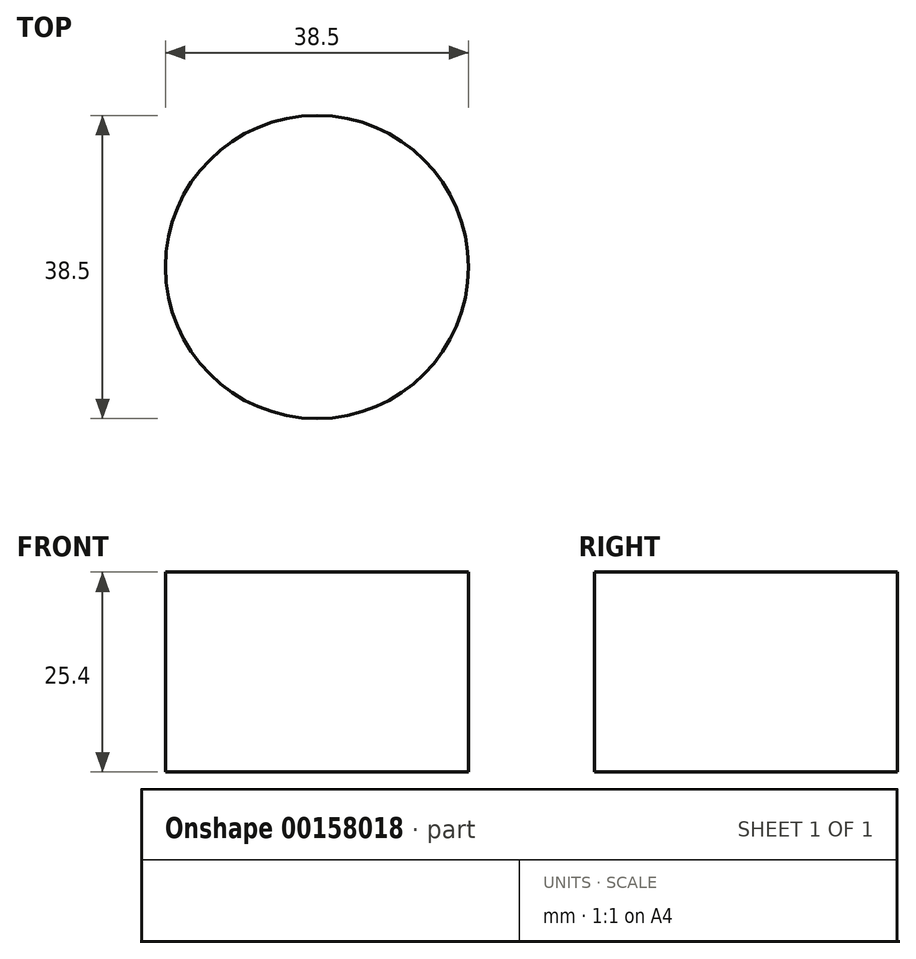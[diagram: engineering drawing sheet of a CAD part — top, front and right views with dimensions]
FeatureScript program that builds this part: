
annotation { "Feature Type Name" : "Feature", "Feature Type Description" : "" }
export const myFeature = defineFeature(function(context is Context, id is Id, definition is map)
    precondition{}
    {
        {
            var Q0;
            Q0=qCreatedBy(makeId("Top.planeOp"),FACE);
            var sketch = newSketch(context, id + "F0", { "sketchPlane" : qUnion([Q0])});
            skCircle(sketch, "E0", {"center": v(0, -15.75) * mm, "radius": 19.25 * mm});
            skCircle(sketch, "E1", {"center": v(-23.5, -39.25) * mm, "radius": 2.5 * mm});
            skCircle(sketch, "E2", {"center": v(-23.5, 7.75) * mm, "radius": 2.5 * mm});
            skCircle(sketch, "E3", {"center": v(23.5, 7.75) * mm, "radius": 2.5 * mm});
            skCircle(sketch, "E4", {"center": v(23.5, -39.25) * mm, "radius": 2.5 * mm});
            skCircle(sketch, "E5", {"center": v(-55.25, 32) * mm, "radius": 2.5 * mm});
            skCircle(sketch, "E6", {"center": v(-33.25, 32) * mm, "radius": 2.5 * mm});
            skCircle(sketch, "E7", {"center": v(-55.25, 8) * mm, "radius": 2.5 * mm});
            skCircle(sketch, "E8", {"center": v(-33.25, 8) * mm, "radius": 2.5 * mm});
            skCircle(sketch, "E9", {"center": v(33.25, 8) * mm, "radius": 2.5 * mm});
            skCircle(sketch, "E10", {"center": v(55.25, 8) * mm, "radius": 2.5 * mm});
            skCircle(sketch, "E11", {"center": v(55.25, 32) * mm, "radius": 2.5 * mm});
            skCircle(sketch, "E12", {"center": v(33.25, 32) * mm, "radius": 2.5 * mm});
            skCircle(sketch, "E13", {"center": v(-53.25, -27) * mm, "radius": 2.5 * mm});
            skCircle(sketch, "E14", {"center": v(-53.25, -2) * mm, "radius": 2.5 * mm});
            skCircle(sketch, "E15", {"center": v(53.25, -27) * mm, "radius": 2.5 * mm});
            skCircle(sketch, "E16", {"center": v(53.25, -2) * mm, "radius": 2.5 * mm});
            skCircle(sketch, "E17", {"center": v(-36.25, -14.5) * mm, "radius": 2.5 * mm});
            skCircle(sketch, "E18", {"center": v(36.25, -14.5) * mm, "radius": 2.5 * mm});
            skCircle(sketch, "E19", {"center": v(34.75, -2.5) * mm, "radius": 3.5 * mm});
            skArc(sketch, "E20", {"start": v(14.75, 38) * mm, "mid": v(13.34, 37.41) * mm, "end": v(12.75, 36) * mm});
            skArc(sketch, "E21", {"start": v(10.75, 30) * mm, "mid": v(12.16, 30.59) * mm, "end": v(12.75, 32) * mm});
            skArc(sketch, "E22", {"start": v(-2.75, 32) * mm, "mid": v(-2.16, 30.59) * mm, "end": v(-0.75, 30) * mm});
            skArc(sketch, "E23", {"start": v(-2.75, 36) * mm, "mid": v(-3.34, 37.41) * mm, "end": v(-4.75, 38) * mm});
            skArc(sketch, "E24", {"start": v(-56.25, 38) * mm, "mid": v(-59.79, 36.54) * mm, "end": v(-61.25, 33) * mm});
            skArc(sketch, "E25", {"start": v(61.25, 33) * mm, "mid": v(59.79, 36.54) * mm, "end": v(56.25, 38) * mm});
            skArc(sketch, "E26", {"start": v(56.25, -42) * mm, "mid": v(59.79, -40.54) * mm, "end": v(61.25, -37) * mm});
            skArc(sketch, "E27", {"start": v(-61.25, -37) * mm, "mid": v(-59.79, -40.54) * mm, "end": v(-56.25, -42) * mm});
            skCircle(sketch, "E28", {"center": v(-15.25, 38) * mm, "radius": 1.5 * mm});
            skArc(sketch, "E29", {"start": v(-9.25, 38) * mm, "mid": v(-15.25, 44) * mm, "end": v(-21.25, 38) * mm});
            skLineSegment(sketch, "E30", {"start": v(-56.25, 38) * mm, "end": v(-21.25, 38) * mm});
            skLineSegment(sketch, "E31", {"start": v(-61.25, 33) * mm, "end": v(-61.25, -37) * mm});
            skLineSegment(sketch, "E32", {"start": v(-56.25, -42) * mm, "end": v(-29.96, -42) * mm});
            skLineSegment(sketch, "E33", {"start": v(61.25, 33) * mm, "end": v(61.25, -37) * mm});
            skLineSegment(sketch, "E34", {"start": v(-26.5, -44) * mm, "end": v(26.5, -44) * mm});
            skLineSegment(sketch, "E35", {"start": v(-26.5, -44) * mm, "end": v(-29.96, -42) * mm});
            skLineSegment(sketch, "E36", {"start": v(26.5, -44) * mm, "end": v(29.96, -42) * mm});
            skLineSegment(sketch, "E37", {"start": v(29.96, -42) * mm, "end": v(56.25, -42) * mm});
            skLineSegment(sketch, "E38", {"start": v(12.75, 36) * mm, "end": v(12.75, 32) * mm});
            skLineSegment(sketch, "E39", {"start": v(-2.75, 36) * mm, "end": v(-2.75, 32) * mm});
            skLineSegment(sketch, "E40", {"start": v(-0.75, 30) * mm, "end": v(10.75, 30) * mm});
            skLineSegment(sketch, "E41", {"start": v(14.75, 38) * mm, "end": v(56.25, 38) * mm});
            skLineSegment(sketch, "E42", {"start": v(-9.25, 38) * mm, "end": v(-4.75, 38) * mm});
            skSolve(sketch);
        }
        {
            var Q0;
            Q0=makeQuery(id+"F0.imprint","IMPRINT",FACE,{"disambiguationData":[TD([[makeQuery(id+"F0.imprint","IMPRINT",EDGE,{"derivedFrom":sQuery(id+"F0.wireOp",EDGE,"E0")}),1.0]])]});
            extrude(context, id + "F1", {"entities" : qUnion([Q0]), "depth" : 25.4 * mm});
        }
    });
